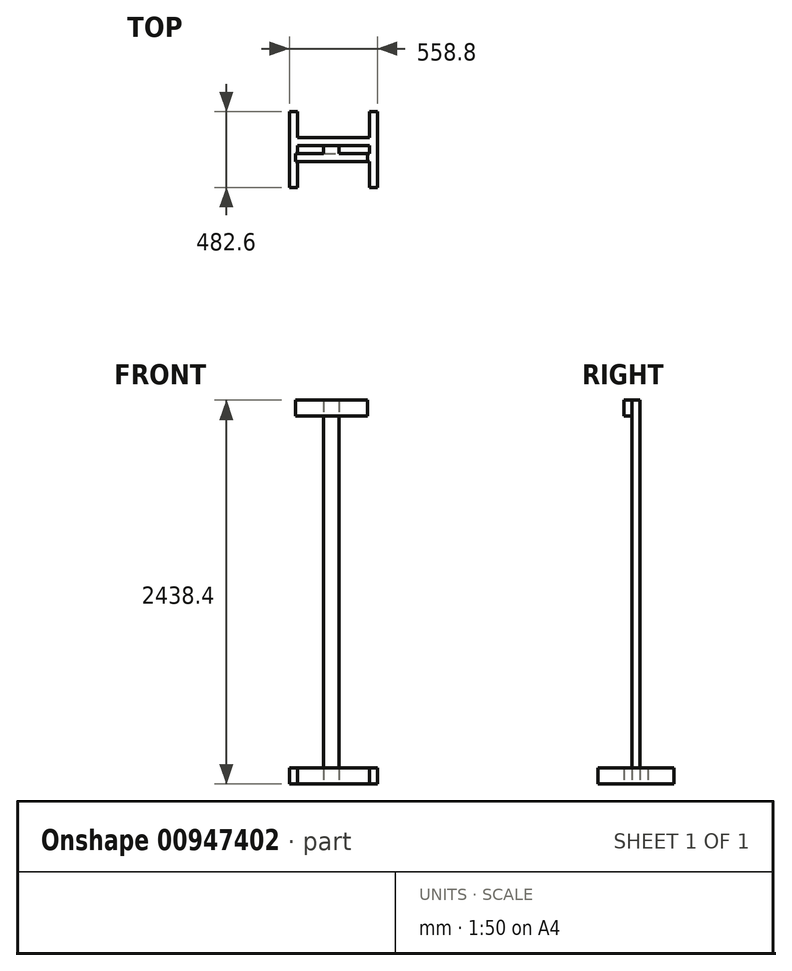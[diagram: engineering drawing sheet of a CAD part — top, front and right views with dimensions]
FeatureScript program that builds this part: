
annotation { "Feature Type Name" : "Feature", "Feature Type Description" : "" }
export const myFeature = defineFeature(function(context is Context, id is Id, definition is map)
    precondition{}
    {
        {
            var Q0;
            Q0=qCreatedBy(makeId("Top.planeOp"),FACE);
            var sketch = newSketch(context, id + "F0", { "sketchPlane" : qUnion([Q0])});
            skLineSegment(sketch, "E0.bottom", {"start": v(-219.26, 105.93) * mm, "end": v(237.94, 105.93) * mm});
            skLineSegment(sketch, "E0.top", {"start": v(-219.26, 55.13) * mm, "end": v(237.94, 55.13) * mm});
            skLineSegment(sketch, "E0.left", {"start": v(-219.26, 105.93) * mm, "end": v(-219.26, 55.13) * mm});
            skLineSegment(sketch, "E0.right", {"start": v(237.94, 105.93) * mm, "end": v(237.94, 55.13) * mm});
            skLineSegment(sketch, "E1.bottom", {"start": v(-219.26, 4.33) * mm, "end": v(237.94, 4.33) * mm});
            skLineSegment(sketch, "E1.top", {"start": v(-219.26, -46.47) * mm, "end": v(237.94, -46.47) * mm});
            skLineSegment(sketch, "E1.left", {"start": v(-219.26, 4.33) * mm, "end": v(-219.26, -46.47) * mm});
            skLineSegment(sketch, "E1.right", {"start": v(237.94, 4.33) * mm, "end": v(237.94, -46.47) * mm});
            skLineSegment(sketch, "E2.bottom", {"start": v(237.94, 271.03) * mm, "end": v(288.74, 271.03) * mm});
            skLineSegment(sketch, "E2.top", {"start": v(237.94, -211.57) * mm, "end": v(288.74, -211.57) * mm});
            skLineSegment(sketch, "E2.left", {"start": v(237.94, 271.03) * mm, "end": v(237.94, -211.57) * mm});
            skLineSegment(sketch, "E2.right", {"start": v(288.74, 271.03) * mm, "end": v(288.74, -211.57) * mm});
            skLineSegment(sketch, "E3.bottom", {"start": v(-270.06, 271.03) * mm, "end": v(-219.26, 271.03) * mm});
            skLineSegment(sketch, "E3.top", {"start": v(-270.06, -211.57) * mm, "end": v(-219.26, -211.57) * mm});
            skLineSegment(sketch, "E3.left", {"start": v(-270.06, 271.03) * mm, "end": v(-270.06, -211.57) * mm});
            skLineSegment(sketch, "E3.right", {"start": v(-219.26, 271.03) * mm, "end": v(-219.26, -211.57) * mm});
            skLineSegment(sketch, "E4", {"start": v(-121.62, 55.13) * mm, "end": v(-121.62, 4.33) * mm, "construction": true});
            skLineSegment(sketch, "E5", {"start": v(237.94, -211.57) * mm, "end": v(237.94, -46.47) * mm});
            skLineSegment(sketch, "E6", {"start": v(9.34, -211.57) * mm, "end": v(9.34, -46.47) * mm, "construction": true});
            skLineSegment(sketch, "E7", {"start": v(9.34, 271.03) * mm, "end": v(9.34, 105.93) * mm, "construction": true});
            skLineSegment(sketch, "E8", {"start": v(9.34, 271.03) * mm, "end": v(237.94, 271.03) * mm, "construction": true});
            skLineSegment(sketch, "E9", {"start": v(9.34, -211.57) * mm, "end": v(237.94, -211.57) * mm, "construction": true});
            skSolve(sketch);
        }
        {
            var Q0;
            Q0 = qSketchRegion(id + "F0", true);
            extrude(context, id + "F1", {"entities" : qUnion([Q0]), "depth" : 101.6 * mm, "offsetDistance" : 25.4 * mm});
        }
        {
            var Q0;
            Q0=qCreatedBy(makeId("Top.planeOp"),FACE);
            var sketch = newSketch(context, id + "F2", { "sketchPlane" : qUnion([Q0])});
            skLineSegment(sketch, "E10.bottom", {"start": v(-51.68, 55.13) * mm, "end": v(46.87, 55.13) * mm});
            skLineSegment(sketch, "E10.top", {"start": v(-51.68, 4.33) * mm, "end": v(46.87, 4.33) * mm});
            skLineSegment(sketch, "E10.left", {"start": v(-51.68, 55.13) * mm, "end": v(-51.68, 4.33) * mm});
            skLineSegment(sketch, "E10.right", {"start": v(46.87, 55.13) * mm, "end": v(46.87, 4.33) * mm});
            skSolve(sketch);
        }
        {
            var Q0;
            Q0 = qSketchRegion(id + "F2", true);
            extrude(context, id + "F3", {"entities" : qUnion([Q0]), "operationType" : NewBodyOperationType.ADD, "depth" : 2438.4 * mm, "offsetDistance" : 25.4 * mm});
        }
        {
            var Q0;
            Q0=makeQuery(id+"F3.opExtrude","SWEPT_FACE",FACE,{"disambiguationData":[OSD([sQuery(id+"F2.wireOp",EDGE,"E10.top")])]});
            var sketch = newSketch(context, id + "F4", { "sketchPlane" : qUnion([Q0])});
            skLineSegment(sketch, "E11.bottom", {"start": v(-231, 2438.4) * mm, "end": v(226.2, 2438.4) * mm});
            skLineSegment(sketch, "E11.top", {"start": v(-231, 2336.8) * mm, "end": v(226.2, 2336.8) * mm});
            skLineSegment(sketch, "E11.left", {"start": v(-231, 2438.4) * mm, "end": v(-231, 2336.8) * mm});
            skLineSegment(sketch, "E11.right", {"start": v(226.2, 2438.4) * mm, "end": v(226.2, 2336.8) * mm});
            skSolve(sketch);
        }
        {
            var Q0;
            Q0 = qSketchRegion(id + "F4", true);
            extrude(context, id + "F5", {"entities" : qUnion([Q0]), "operationType" : NewBodyOperationType.ADD, "depth" : 50.8 * mm, "offsetDistance" : 25.4 * mm});
        }
    });
